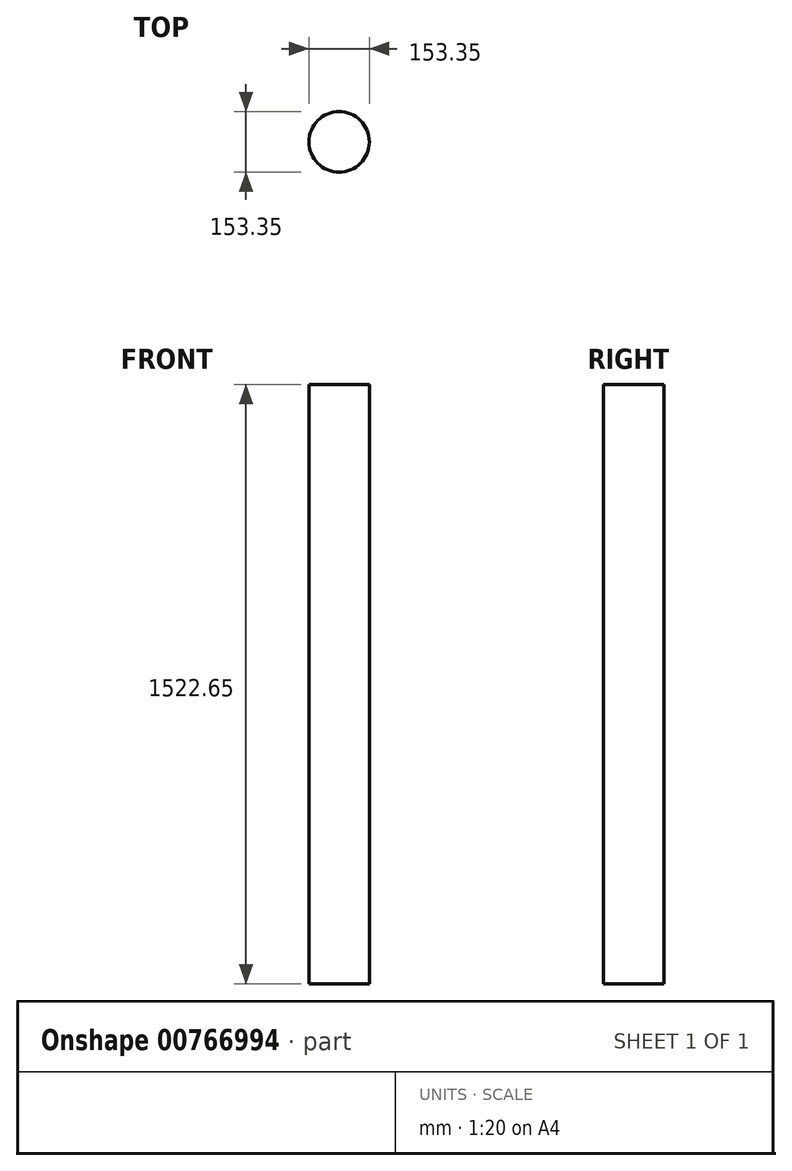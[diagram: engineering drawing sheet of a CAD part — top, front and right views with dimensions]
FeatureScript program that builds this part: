
annotation { "Feature Type Name" : "Feature", "Feature Type Description" : "" }
export const myFeature = defineFeature(function(context is Context, id is Id, definition is map)
    precondition{}
    {
        {
            var Q0;
            Q0=qCreatedBy(makeId("Top.planeOp"),FACE);
            var sketch = newSketch(context, id + "F0", { "sketchPlane" : qUnion([Q0])});
            skCircle(sketch, "E0", {"center": v(1.79, -6.06) * mm, "radius": 76.67 * mm});
            skSolve(sketch);
        }
        {
            var Q0;
            Q0=makeQuery(id+"F0.imprint","IMPRINT",FACE,{"disambiguationData":[TD([[makeQuery(id+"F0.imprint","IMPRINT",EDGE,{"derivedFrom":sQuery(id+"F0.wireOp",EDGE,"E0")}),1.0]])]});
            var sketch = newSketch(context, id + "F1", { "sketchPlane" : qUnion([Q0])});
            skSolve(sketch);
        }
        {
            var Q0;
            Q0=makeQuery(id+"F1.imprint","IMPRINT",FACE,{"disambiguationData":[TD([[makeQuery(id+"F1.imprint","IMPRINT",EDGE,{"derivedFrom":makeQuery(id+"F0.imprint","IMPRINT",EDGE,{"derivedFrom":sQuery(id+"F0.wireOp",EDGE,"E0")})}),1.0]])]});
            extrude(context, id + "F2", {"entities" : qUnion([Q0]), "depth" : 1522.65 * mm, "offsetDistance" : 25.4 * mm});
        }
    });
